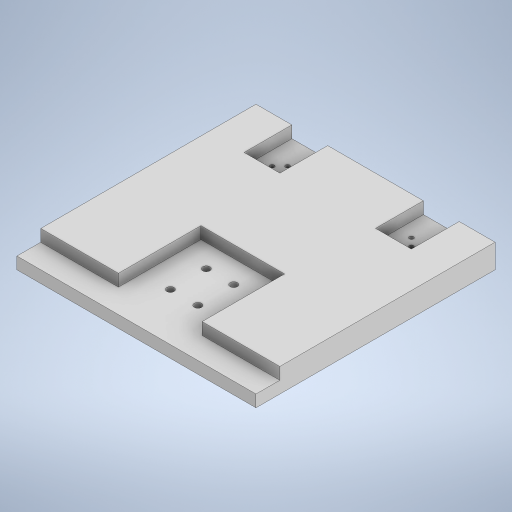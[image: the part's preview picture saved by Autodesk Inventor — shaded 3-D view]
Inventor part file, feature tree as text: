
AUTODESK INVENTOR PART (.ipt)
format: ipt  version: 2023 (Build 270158000, 158)  size: 304,640 bytes
history: native  units: mm
features: sketch x5, extrude x4, other x1, hole x1
ambient origin geometry x8: Origin, YZ Plane, XZ Plane, XY Plane, X Axis, Y Axis, Z Axis, Center Point
bodies: Body1 (feature_tree)
feature tree (11):
  other  "Sólido1"
  extrude  "Extrusión1"  Depth=200.0mm
  extrude  "Extrusión2"  Depth=10.0mm TaperAngle=0.0deg
  extrude  "Extrusión3"  Depth=20.0mm
  hole  "Agujero1"  [1 undecoded]
  extrude  "Extrusión4"  Depth=40.0mm
  sketch  "Boceto1"  dims[d0=200.0mm d1=200.0mm]
  sketch  "Boceto2"  dims[d2=20.0mm d3=0.0mm]
  sketch  "Boceto3"  dims[d4=20.0mm d5=20.0mm d6=30.0mm d7=30.0mm d8=20.0mm d9=35.0mm d10=35.0mm d11=69.0mm d12=10.0mm d13=0.0mm]
  sketch  "Boceto4"  dims[d14=20.0mm d15=0.0mm]
  sketch  "Boceto5"  dims[d16=3.5mm d18=1.75mm d19=1.75mm d20=1.75mm d21=1.75mm d22=10.0mm d23=10.0mm d25=20.0mm d26=40.0mm d27=40.0mm d28=3.5mm d29=6.0mm d30=4.0mm d31=2.0mm d32=90.0deg d33=8.0mm d34=20.594885mm d38=10.0mm d39=10.0mm d40=40.0mm d41=10.0mm d42=0.0mm]
note: 1 required parameter value undecoded (feature->parameter linkage not recoverable at this tier; creation-order binding heuristic only, values carry confidence <= 0.55)
